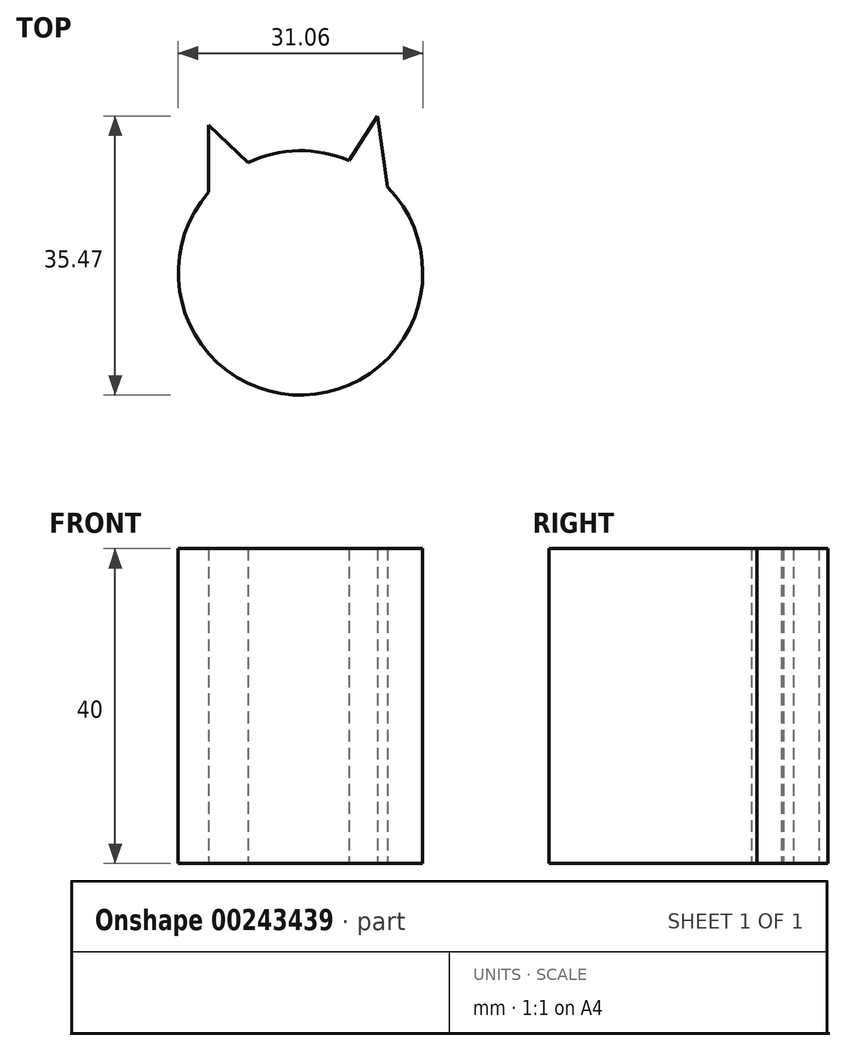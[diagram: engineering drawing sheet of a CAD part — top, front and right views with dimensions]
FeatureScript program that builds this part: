
annotation { "Feature Type Name" : "Feature", "Feature Type Description" : "" }
export const myFeature = defineFeature(function(context is Context, id is Id, definition is map)
    precondition{}
    {
        {
            var Q0;
            Q0=qCreatedBy(makeId("Top.planeOp"),FACE);
            var sketch = newSketch(context, id + "F0", { "sketchPlane" : qUnion([Q0])});
            skCircle(sketch, "E0", {"center": v(0, 0) * mm, "radius": 15.53 * mm});
            skLineSegment(sketch, "E1", {"start": v(-11.67, 10.24) * mm, "end": v(-11.67, 18.8) * mm});
            skLineSegment(sketch, "E2", {"start": v(-11.67, 18.8) * mm, "end": v(-6.66, 14.03) * mm});
            skLineSegment(sketch, "E3", {"start": v(6.16, 14.25) * mm, "end": v(9.75, 19.94) * mm});
            skLineSegment(sketch, "E4", {"start": v(9.75, 19.94) * mm, "end": v(11.05, 10.9) * mm});
            skSolve(sketch);
        }
        {
            var Q0;
            {var subQ0=sQuery(id+"F0.wireOp",EDGE,"E0");var subQ1=makeQuery(id+"F0.imprint","INTERSECT",VERTEX,{"derivedFrom":[subQ0,sQuery(id+"F0.wireOp",EDGE,"E3")]});Q0=makeQuery(id+"F0.imprint","IMPRINT",FACE,{"disambiguationData":[TD([[makeQuery(id+"F0.imprint","IMPRINT",EDGE,{"disambiguationData":[TD([[subQ1,1.0]])],"derivedFrom":subQ0}),1.0]])]});}
            var Q1;
            {var subQ0=sQuery(id+"F0.wireOp",EDGE,"E1");Q1=makeQuery(id+"F0.imprint","IMPRINT",FACE,{"disambiguationData":[TD([[makeQuery(id+"F0.imprint","IMPRINT",EDGE,{"derivedFrom":subQ0}),-1.0]])]});}
            var Q2;
            {var subQ0=sQuery(id+"F0.wireOp",EDGE,"E3");Q2=makeQuery(id+"F0.imprint","IMPRINT",FACE,{"disambiguationData":[TD([[makeQuery(id+"F0.imprint","IMPRINT",EDGE,{"derivedFrom":subQ0}),-1.0]])]});}
            extrude(context, id + "F1", {"entities" : qUnion([Q0, Q1, Q2]), "depth" : 40 * mm});
        }
    });
